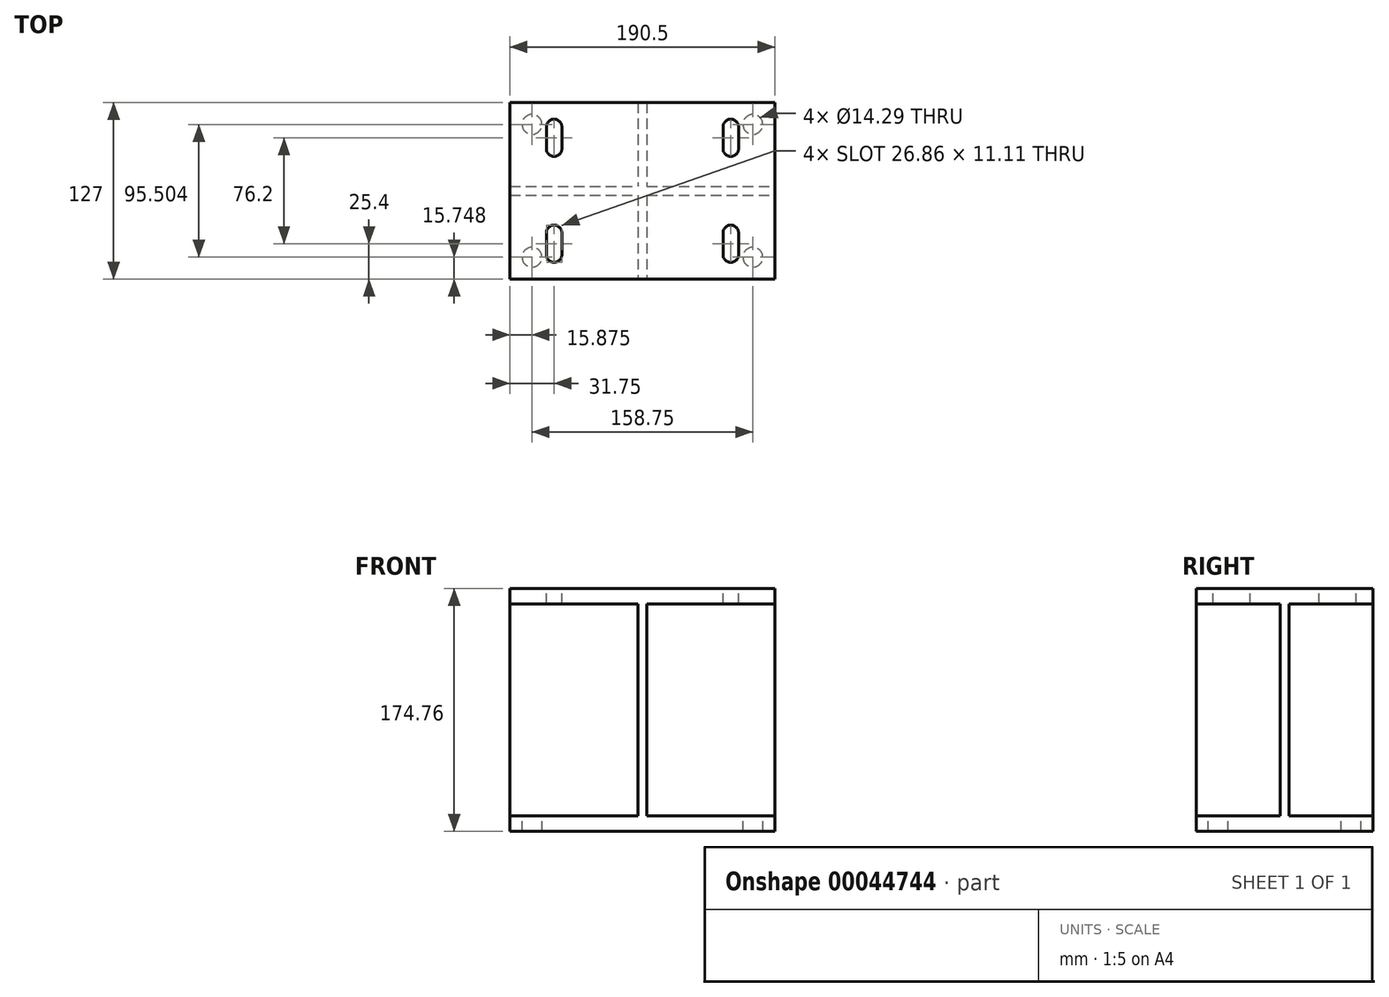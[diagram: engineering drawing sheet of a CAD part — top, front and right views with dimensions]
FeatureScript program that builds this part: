
annotation { "Feature Type Name" : "Feature", "Feature Type Description" : "" }
export const myFeature = defineFeature(function(context is Context, id is Id, definition is map)
    precondition{}
    {
        {
            var Q0;
            Q0=qCreatedBy(makeId("Top.planeOp"),FACE);
            var sketch = newSketch(context, id + "F0", { "sketchPlane" : qUnion([Q0])});
            skLineSegment(sketch, "E0.rect.bottom", {"start": v(-95.25, 63.5) * mm, "end": v(95.25, 63.5) * mm});
            skLineSegment(sketch, "E0.rect.top", {"start": v(-95.25, -63.5) * mm, "end": v(95.25, -63.5) * mm});
            skLineSegment(sketch, "E0.rect.left", {"start": v(-95.25, 63.5) * mm, "end": v(-95.25, -63.5) * mm});
            skLineSegment(sketch, "E0.rect.right", {"start": v(95.25, 63.5) * mm, "end": v(95.25, -63.5) * mm});
            skPoint(sketch, "E0.rect.middle", {"position": v(0, 0) * mm});
            skLineSegment(sketch, "E1", {"start": v(0, 83.52) * mm, "end": v(0, -77.8) * mm, "construction": true});
            skLineSegment(sketch, "E2", {"start": v(-118.93, 0) * mm, "end": v(113.92, 0) * mm, "construction": true});
            skLineSegment(sketch, "E3.0", {"start": v(-118.93, 47.75) * mm, "end": v(113.92, 47.75) * mm, "construction": true});
            skLineSegment(sketch, "E4.0", {"start": v(-79.38, 83.52) * mm, "end": v(-79.37, -77.8) * mm, "construction": true});
            skCircle(sketch, "E5", {"center": v(-79.37, 47.75) * mm, "radius": 7.14 * mm});
            skCircle(sketch, "E6.MirrorC", {"center": v(79.37, 47.75) * mm, "radius": 7.14 * mm});
            skCircle(sketch, "E7.MirrorC", {"center": v(-79.37, -47.75) * mm, "radius": 7.14 * mm});
            skCircle(sketch, "E8.MirrorC", {"center": v(79.37, -47.75) * mm, "radius": 7.14 * mm});
            skSolve(sketch);
        }
        {
            var Q0;
            Q0 = qSketchRegion(id + "F0", true);
            extrude(context, id + "F1", {"entities" : qUnion([Q0]), "oppositeDirection" : true, "depth" : 11.18 * mm});
        }
        {
            var Q0;
            Q0=makeQuery(id+"F1.opExtrude","CAP_FACE",FACE,{"disambiguationData":[OSD([sQuery(id+"F0.wireOp",EDGE,"E0.rect.bottom"),sQuery(id+"F0.wireOp",EDGE,"E0.rect.top"),sQuery(id+"F0.wireOp",EDGE,"E0.rect.left"),sQuery(id+"F0.wireOp",EDGE,"E0.rect.right"),sQuery(id+"F0.wireOp",EDGE,"E5"),sQuery(id+"F0.wireOp",EDGE,"E6.MirrorC"),sQuery(id+"F0.wireOp",EDGE,"E7.MirrorC"),sQuery(id+"F0.wireOp",EDGE,"E8.MirrorC")])],"isStart":true});
            var sketch = newSketch(context, id + "F2", { "sketchPlane" : qUnion([Q0])});
            skLineSegment(sketch, "E9", {"start": v(0, 94.97) * mm, "end": v(0, -96.04) * mm, "construction": true});
            skLineSegment(sketch, "E10", {"start": v(-122.5, 0) * mm, "end": v(124.65, 0) * mm, "construction": true});
            skLineSegment(sketch, "E11.0", {"start": v(-3.18, 94.97) * mm, "end": v(-3.17, -96.04) * mm, "construction": true});
            skLineSegment(sketch, "E12.0", {"start": v(-122.5, 3.18) * mm, "end": v(124.65, 3.18) * mm, "construction": true});
            skLineSegment(sketch, "E13.bottom", {"start": v(-3.17, 63.5) * mm, "end": v(3.18, 63.5) * mm});
            skLineSegment(sketch, "E13.top", {"start": v(-3.17, -63.5) * mm, "end": v(3.18, -63.5) * mm});
            skLineSegment(sketch, "E13.left", {"start": v(-3.17, 63.5) * mm, "end": v(-3.17, -63.5) * mm});
            skLineSegment(sketch, "E13.right", {"start": v(3.18, 63.5) * mm, "end": v(3.18, -63.5) * mm});
            skLineSegment(sketch, "E14.bottom", {"start": v(-95.25, 3.18) * mm, "end": v(95.25, 3.18) * mm});
            skLineSegment(sketch, "E14.top", {"start": v(-95.25, -3.18) * mm, "end": v(95.25, -3.18) * mm});
            skLineSegment(sketch, "E14.left", {"start": v(-95.25, 3.18) * mm, "end": v(-95.25, -3.17) * mm});
            skLineSegment(sketch, "E14.right", {"start": v(95.25, 3.18) * mm, "end": v(95.25, -3.18) * mm});
            skSolve(sketch);
        }
        {
            var Q0;
            Q0 = qSketchRegion(id + "F2", true);
            extrude(context, id + "F3", {"entities" : qUnion([Q0]), "operationType" : NewBodyOperationType.ADD, "depth" : 152.4 * mm});
        }
        {
            var Q0;
            Q0=makeQuery(id+"F3.opExtrude","CAP_FACE",FACE,{"disambiguationData":[OSD([sQuery(id+"F2.wireOp",EDGE,"E13.bottom"),sQuery(id+"F2.wireOp",EDGE,"E13.top"),sQuery(id+"F2.wireOp",EDGE,"E13.left"),sQuery(id+"F2.wireOp",EDGE,"E13.right"),sQuery(id+"F2.wireOp",EDGE,"E14.bottom"),sQuery(id+"F2.wireOp",EDGE,"E14.top"),sQuery(id+"F2.wireOp",EDGE,"E14.left"),sQuery(id+"F2.wireOp",EDGE,"E14.right")])],"isStart":false});
            var sketch = newSketch(context, id + "F4", { "sketchPlane" : qUnion([Q0])});
            skLineSegment(sketch, "E15.0", {"start": v(-95.25, 63.5) * mm, "end": v(95.25, 63.5) * mm});
            skLineSegment(sketch, "E16.0", {"start": v(-95.25, 63.5) * mm, "end": v(-95.25, -63.5) * mm});
            skLineSegment(sketch, "E17.0", {"start": v(-95.25, -63.5) * mm, "end": v(95.25, -63.5) * mm});
            skLineSegment(sketch, "E18.0", {"start": v(95.25, 63.5) * mm, "end": v(95.25, -63.5) * mm});
            skPoint(sketch, "E19.orphan", {"position": v(-3.17, 63.5) * mm});
            skPoint(sketch, "E20.orphan", {"position": v(95.25, -3.18) * mm});
            skPoint(sketch, "E21.orphan", {"position": v(-3.17, -63.5) * mm});
            skPoint(sketch, "E22.orphan", {"position": v(-95.25, -63.5) * mm});
            skPoint(sketch, "E23.orphan", {"position": v(-95.25, 3.18) * mm});
            skSolve(sketch);
        }
        {
            var Q0;
            Q0 = qSketchRegion(id + "F4", true);
            extrude(context, id + "F5", {"entities" : qUnion([Q0]), "operationType" : NewBodyOperationType.ADD, "depth" : 11.18 * mm});
        }
        {
            var Q0;
            Q0=makeQuery(id+"F5.opExtrude","CAP_FACE",FACE,{"disambiguationData":[OSD([sQuery(id+"F4.wireOp",EDGE,"E15.0"),sQuery(id+"F4.wireOp",EDGE,"E16.0"),sQuery(id+"F4.wireOp",EDGE,"E17.0"),sQuery(id+"F4.wireOp",EDGE,"E18.0")])],"isStart":false});
            var sketch = newSketch(context, id + "F6", { "sketchPlane" : qUnion([Q0])});
            skLineSegment(sketch, "E24", {"start": v(0, 89.84) * mm, "end": v(0, -94.13) * mm, "construction": true});
            skLineSegment(sketch, "E25", {"start": v(-123.37, 0) * mm, "end": v(124.53, 0) * mm, "construction": true});
            skLineSegment(sketch, "E26.0", {"start": v(-63.5, 89.84) * mm, "end": v(-63.5, -94.13) * mm, "construction": true});
            skLineSegment(sketch, "E27.0", {"start": v(-123.37, -38.1) * mm, "end": v(124.53, -38.1) * mm, "construction": true});
            skLineSegment(sketch, "E28.0", {"start": v(-123.37, -30.23) * mm, "end": v(124.53, -30.23) * mm, "construction": true});
            skLineSegment(sketch, "E29.0", {"start": v(-123.37, -45.97) * mm, "end": v(124.53, -45.97) * mm, "construction": true});
            skLineSegment(sketch, "E30", {"start": v(-63.5, -30.23) * mm, "end": v(-63.5, -45.97) * mm});
            skArc(sketch, "E31.0.startCap", {"start": v(-69.06, -30.23) * mm, "mid": v(-63.5, -24.67) * mm, "end": v(-57.94, -30.23) * mm});
            skArc(sketch, "E31.0.endCap", {"start": v(-57.94, -45.97) * mm, "mid": v(-63.5, -51.53) * mm, "end": v(-69.06, -45.97) * mm});
            skLineSegment(sketch, "E31.0.left", {"start": v(-57.94, -30.23) * mm, "end": v(-57.94, -45.97) * mm});
            skLineSegment(sketch, "E31.0.right", {"start": v(-69.06, -30.23) * mm, "end": v(-69.06, -45.97) * mm});
            skArc(sketch, "E32.MirrorCS", {"start": v(69.06, -30.23) * mm, "mid": v(63.5, -24.67) * mm, "end": v(57.94, -30.23) * mm});
            skLineSegment(sketch, "E33.MirrorCS", {"start": v(63.5, -30.23) * mm, "end": v(63.5, -45.97) * mm});
            skArc(sketch, "E34.MirrorCS", {"start": v(57.94, -45.97) * mm, "mid": v(63.5, -51.53) * mm, "end": v(69.06, -45.97) * mm});
            skLineSegment(sketch, "E35.MirrorCS", {"start": v(57.94, -30.23) * mm, "end": v(57.94, -45.97) * mm});
            skLineSegment(sketch, "E36.MirrorCS", {"start": v(69.06, -30.23) * mm, "end": v(69.06, -45.97) * mm});
            skLineSegment(sketch, "E37.MirrorCS", {"start": v(-69.06, 30.23) * mm, "end": v(-69.06, 45.97) * mm});
            skLineSegment(sketch, "E38.MirrorCS", {"start": v(-57.94, 30.23) * mm, "end": v(-57.94, 45.97) * mm});
            skArc(sketch, "E39.MirrorCS", {"start": v(-69.06, 30.23) * mm, "mid": v(-63.5, 24.67) * mm, "end": v(-57.94, 30.23) * mm});
            skLineSegment(sketch, "E40.MirrorCS", {"start": v(-63.5, 30.23) * mm, "end": v(-63.5, 45.97) * mm});
            skArc(sketch, "E41.MirrorCS", {"start": v(69.06, 30.23) * mm, "mid": v(63.5, 24.67) * mm, "end": v(57.94, 30.23) * mm});
            skLineSegment(sketch, "E42.MirrorCS", {"start": v(63.5, 30.23) * mm, "end": v(63.5, 45.97) * mm});
            skArc(sketch, "E43.MirrorCS", {"start": v(-57.94, 45.97) * mm, "mid": v(-63.5, 51.53) * mm, "end": v(-69.06, 45.97) * mm});
            skArc(sketch, "E44.MirrorCS", {"start": v(57.94, 45.97) * mm, "mid": v(63.5, 51.53) * mm, "end": v(69.06, 45.97) * mm});
            skLineSegment(sketch, "E45.MirrorCS", {"start": v(57.94, 30.23) * mm, "end": v(57.94, 45.97) * mm});
            skLineSegment(sketch, "E46.MirrorCS", {"start": v(69.06, 30.23) * mm, "end": v(69.06, 45.97) * mm});
            skSolve(sketch);
        }
        {
            var Q0;
            Q0 = qSketchRegion(id + "F6", true);
            extrude(context, id + "F7", {"entities" : qUnion([Q0]), "operationType" : NewBodyOperationType.REMOVE, "oppositeDirection" : true, "depth" : 25.4 * mm});
        }
    });
